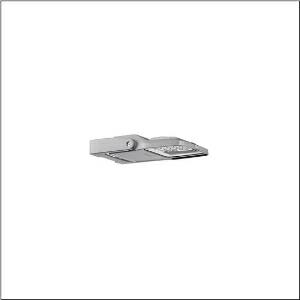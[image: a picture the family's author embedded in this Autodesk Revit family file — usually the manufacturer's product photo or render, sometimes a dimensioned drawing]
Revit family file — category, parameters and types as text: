
# Revit family: floodlight_fl_21_iq_micro___pl61_5xa7762a4c2a_69cd
name_source: partatom
category: Lighting Fixtures
units: mm (PartAtom-declared; Revit-internal decimal feet)

## family parameters
Cut with Voids When Loaded = No
Host = Face
Light Source = No
Part Type = Normal
Room Calculation Point = No
Round Connector Dimension = Use Diameter
Shared = No

## types (1)
- --- (1 x LED, 3030 lm, 23.1 W, 4000K)
    Apparent Load = 23 VA
    CIE Flux Codes = 33 65 98 100 100
    Color Rendering = 70
    Color Temperature = 4000K
    Default Elevation = 1800 mm
    Description = Floodlight FL 21 iQ micro, floodlight, primary light control with lens, of PMMA, primary optical cover: protective disc, of toughened safety glass, transparent, light distribution: PL61, light emission: direct distribution, installation type: surface-mounted, LED, High Power LED, rated luminous flux: 3.030lm, luminous efficacy: 131lm/W, light colour: 740, colour temperature: 4000K, control gear: iQ Street-Remote/DALI, control: Auto-Match, Temp-Guard, Night-Set, Smart-Wire, Desk-Remote (wireless, voltage-free reading and setting of iQ features in the workshop via application-optimized NFC function/RFID function), optimised constant luminous flux control (CLO 2.0), Street-Remote, with terminal, 6-pole, mains connection: 220..240V, AC, 50/60Hz, start of lifetime: 23W, end of service life: 24W, reduction: 11W, luminaire housing, of diecast aluminium, powder-coated, Siteco® metallic grey (DB 702S), corrosivity category C5 mid according to DIN EN ISO 12944, suitable for swimming pools, chlorine-resistant, sealing non-destructively replaceable, design bracket, of diecast aluminium, powder-coated, Siteco® metallic grey (DB 702S), protection rating (complete): IP66, insulation class (complete): insulation class II (safety insulation), certification: CE, ENEC, VDE, protection symbol: D, impact resistance: IK07, permissible operating ambient temperature: -40..+40°C, permissible operating ambient temperature for outdoor applications: -40..+50°C, standard: DIN EN 12944, LABS conformity tested according to VDMA 24364:2018-05, packaging unit: 1 piece

Light Distribution: PL61
    Height = 65 mm
    Lamp = 1 x LED
    Lamp Light Flux = 3030 lm
    Lamp Power = 23.1 W
    Lamp count = 1
    Length = 312 mm
    Luminous efficacy = 131 lm/W
    Manufacturer = Siteco
    ModVariant = No
    Model = 5XA7762A4C2A
    Mounting Place = Wall
    Mounting Type = Surface mounted
    Number of Poles = 1
    OnlyDefault = Yes
    Power Factor = 1
    Product Name = Floodlight FL 21 iQ micro | PL61
    Product group = floodlight | wall mounted
    ProductGroupID = 2001
    Protection Class = Protection class II
    Protection Degree = IP 66
    RLX_Detail_Level = 1
    RLX_Emergency_Light_Flux = 0 lm
    RLX_Emergency_Type = 0
    RLX_Emergency_Type_DB = No
    RlxData = <blob elided: 97565 chars, md5=9dbe84c5>
    Socket = socket
    Standby Power = 0 W
    System Light Flux = 3030 lm
    System Power = 23 W
    Type Comments = factory setting: luminous flux: 100 % | dim-lin: 254 | 455 mA
    Type Image = l_1006878.jpg
    URL = http://relux.com
    VarID = @adj_194296
    Voltage = 0 V
    Weight = 0.00 kg
    Width = 230 mm

## geometry (parser evidence)
native form markers: Blend x4, Sweep x11
no freeform markers — native parametric forms only
